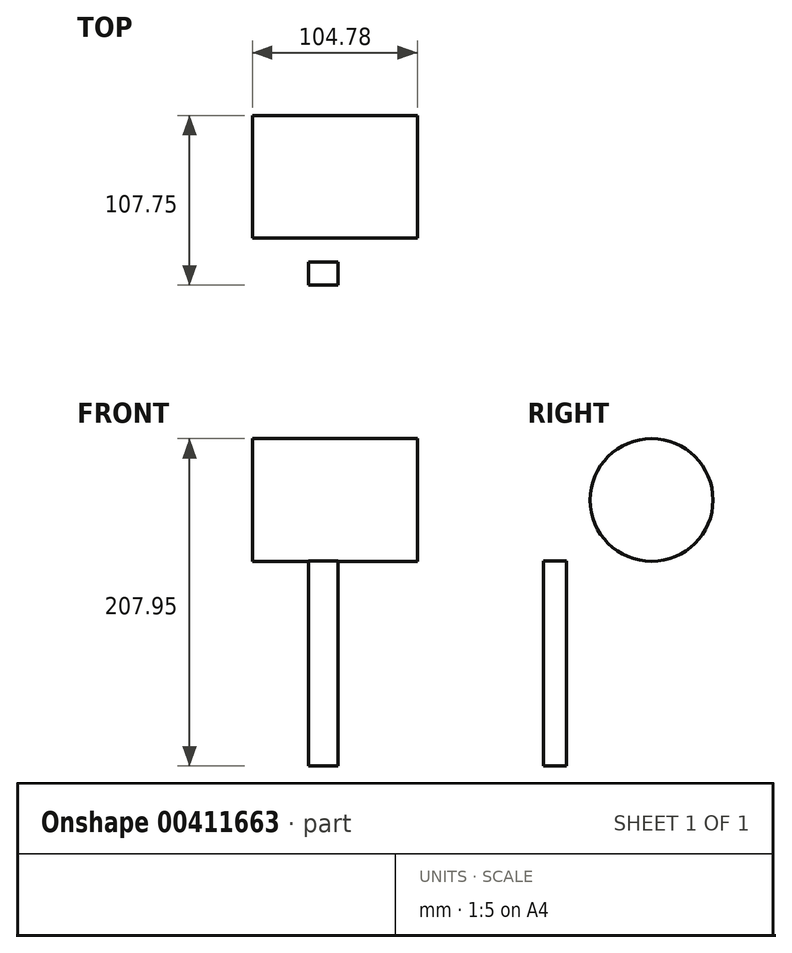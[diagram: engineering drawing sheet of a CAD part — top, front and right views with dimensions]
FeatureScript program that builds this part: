
annotation { "Feature Type Name" : "Feature", "Feature Type Description" : "" }
export const myFeature = defineFeature(function(context is Context, id is Id, definition is map)
    precondition{}
    {
        {
            var Q0;
            Q0=qCreatedBy(makeId("Top.planeOp"),FACE);
            var sketch = newSketch(context, id + "F0", { "sketchPlane" : qUnion([Q0])});
            skLineSegment(sketch, "E0.bottom", {"start": v(-50.48, -54.06) * mm, "end": v(-69.3, -54.06) * mm});
            skLineSegment(sketch, "E0.top", {"start": v(-50.48, -68.76) * mm, "end": v(-69.3, -68.76) * mm});
            skLineSegment(sketch, "E0.left", {"start": v(-50.48, -54.06) * mm, "end": v(-50.48, -68.76) * mm});
            skLineSegment(sketch, "E0.right", {"start": v(-69.3, -54.06) * mm, "end": v(-69.3, -68.76) * mm});
            skSolve(sketch);
        }
        {
            var Q0;
            Q0=makeQuery(id+"F0.imprint","IMPRINT",FACE,{"disambiguationData":[TD([[makeQuery(id+"F0.imprint","IMPRINT",EDGE,{"derivedFrom":sQuery(id+"F0.wireOp",EDGE,"E0.bottom")}),1.0]])]});
            extrude(context, id + "F1", {"entities" : qUnion([Q0]), "oppositeDirection" : true, "depth" : 104.77 * mm, "hasSecondDirection" : true, "secondDirectionOppositeDirection" : false, "secondDirectionDepth" : 25.4 * mm});
        }
        {
            var Q0;
            Q0=qCreatedBy(makeId("Right.planeOp"),FACE);
            var sketch = newSketch(context, id + "F2", { "sketchPlane" : qUnion([Q0])});
            skCircle(sketch, "E1", {"center": v(0, 64.18) * mm, "radius": 39 * mm});
            skSolve(sketch);
        }
        {
            var Q0;
            Q0 = qSketchRegion(id + "F2", true);
            extrude(context, id + "F3", {"entities" : qUnion([Q0]), "oppositeDirection" : true, "depth" : 104.77 * mm});
        }
    });
